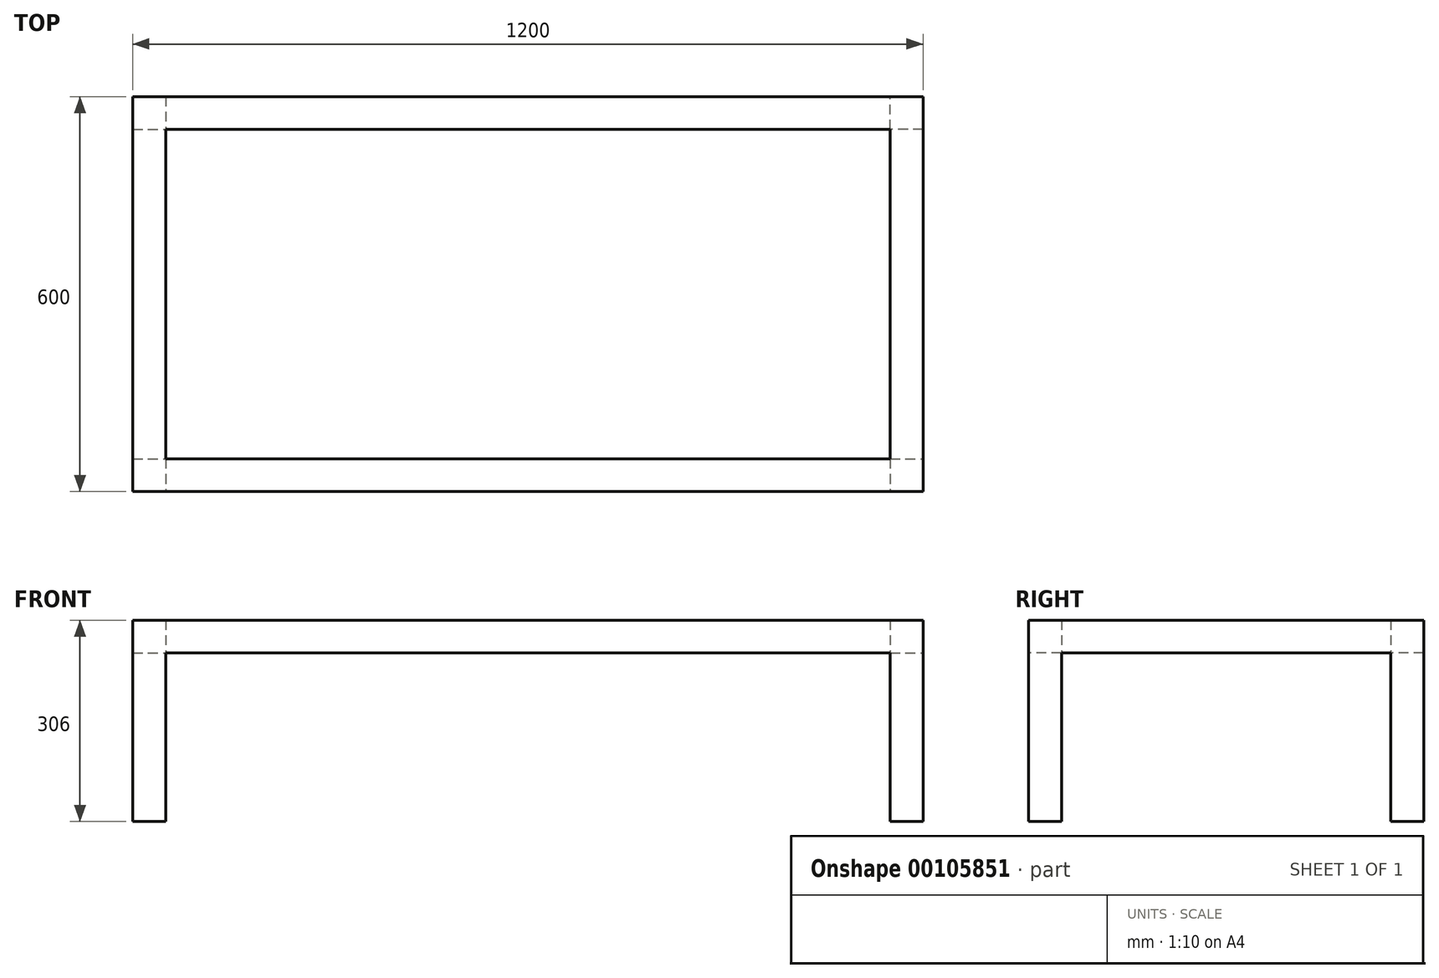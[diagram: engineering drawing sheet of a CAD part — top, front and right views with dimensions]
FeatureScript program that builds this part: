
annotation { "Feature Type Name" : "Feature", "Feature Type Description" : "" }
export const myFeature = defineFeature(function(context is Context, id is Id, definition is map)
    precondition{}
    {
        {
            var Q0;
            Q0=qCreatedBy(makeId("Top.planeOp"),FACE);
            var sketch = newSketch(context, id + "F0", { "sketchPlane" : qUnion([Q0])});
            skLineSegment(sketch, "E0.bottom", {"start": v(0, 0) * mm, "end": v(50, 0) * mm});
            skLineSegment(sketch, "E0.top", {"start": v(0, -50) * mm, "end": v(50, -50) * mm});
            skLineSegment(sketch, "E0.left", {"start": v(0, 0) * mm, "end": v(0, -50) * mm});
            skLineSegment(sketch, "E0.right", {"start": v(50, 0) * mm, "end": v(50, -50) * mm});
            skLineSegment(sketch, "E1.bottom", {"start": v(0, 550) * mm, "end": v(50, 550) * mm});
            skLineSegment(sketch, "E1.top", {"start": v(0, 500) * mm, "end": v(50, 500) * mm});
            skLineSegment(sketch, "E1.left", {"start": v(0, 550) * mm, "end": v(0, 500) * mm});
            skLineSegment(sketch, "E1.right", {"start": v(50, 550) * mm, "end": v(50, 500) * mm});
            skLineSegment(sketch, "E2.bottom", {"start": v(1150, 0) * mm, "end": v(1200, 0) * mm});
            skLineSegment(sketch, "E2.top", {"start": v(1150, -50) * mm, "end": v(1200, -50) * mm});
            skLineSegment(sketch, "E2.left", {"start": v(1150, 0) * mm, "end": v(1150, -50) * mm});
            skLineSegment(sketch, "E2.right", {"start": v(1200, 0) * mm, "end": v(1200, -50) * mm});
            skLineSegment(sketch, "E3.bottom", {"start": v(1200, 500) * mm, "end": v(1150, 500) * mm});
            skLineSegment(sketch, "E3.top", {"start": v(1200, 550) * mm, "end": v(1150, 550) * mm});
            skLineSegment(sketch, "E3.left", {"start": v(1200, 500) * mm, "end": v(1200, 550) * mm});
            skLineSegment(sketch, "E3.right", {"start": v(1150, 500) * mm, "end": v(1150, 550) * mm});
            skSolve(sketch);
        }
        {
            var Q0;
            Q0 = qSketchRegion(id + "F0", true);
            extrude(context, id + "F1", {"entities" : qUnion([Q0]), "depth" : 256 * mm});
        }
        {
            var Q0;
            Q0=makeQuery(id+"F1.opExtrude","CAP_FACE",FACE,{"disambiguationData":[OSD([sQuery(id+"F0.wireOp",EDGE,"E0.bottom"),sQuery(id+"F0.wireOp",EDGE,"E0.top"),sQuery(id+"F0.wireOp",EDGE,"E0.left"),sQuery(id+"F0.wireOp",EDGE,"E0.right")])],"isStart":false});
            var sketch = newSketch(context, id + "F2", { "sketchPlane" : qUnion([Q0])});
            skLineSegment(sketch, "E4.bottom", {"start": v(50, 0) * mm, "end": v(1150, 0) * mm});
            skLineSegment(sketch, "E4.top", {"start": v(0, -50) * mm, "end": v(1200, -50) * mm});
            skLineSegment(sketch, "E4.left", {"start": v(0, 0) * mm, "end": v(0, -50) * mm});
            skLineSegment(sketch, "E4.right", {"start": v(1200, 0) * mm, "end": v(1200, -50) * mm});
            skLineSegment(sketch, "E5.bottom", {"start": v(1200, -50) * mm, "end": v(1150, -50) * mm});
            skLineSegment(sketch, "E5.top", {"start": v(1200, 550) * mm, "end": v(1150, 550) * mm});
            skLineSegment(sketch, "E5.left", {"start": v(1200, -50) * mm, "end": v(1200, 550) * mm});
            skLineSegment(sketch, "E5.right", {"start": v(1150, 0) * mm, "end": v(1150, 500) * mm});
            skLineSegment(sketch, "E6.bottom", {"start": v(1200, 550) * mm, "end": v(0, 550) * mm});
            skLineSegment(sketch, "E6.top", {"start": v(1150, 500) * mm, "end": v(50, 500) * mm});
            skLineSegment(sketch, "E6.left", {"start": v(1200, 550) * mm, "end": v(1200, 500) * mm});
            skLineSegment(sketch, "E6.right", {"start": v(0, 550) * mm, "end": v(0, 500) * mm});
            skLineSegment(sketch, "E7.bottom", {"start": v(0, 550) * mm, "end": v(50, 550) * mm});
            skLineSegment(sketch, "E7.top", {"start": v(0, -50) * mm, "end": v(50, -50) * mm});
            skLineSegment(sketch, "E7.left", {"start": v(0, 550) * mm, "end": v(0, -50) * mm});
            skLineSegment(sketch, "E7.right", {"start": v(50, 500) * mm, "end": v(50, 0) * mm});
            skSolve(sketch);
        }
        {
            var Q0;
            Q0 = qSketchRegion(id + "F2", true);
            extrude(context, id + "F3", {"entities" : qUnion([Q0]), "operationType" : NewBodyOperationType.ADD, "depth" : 50 * mm});
        }
    });
